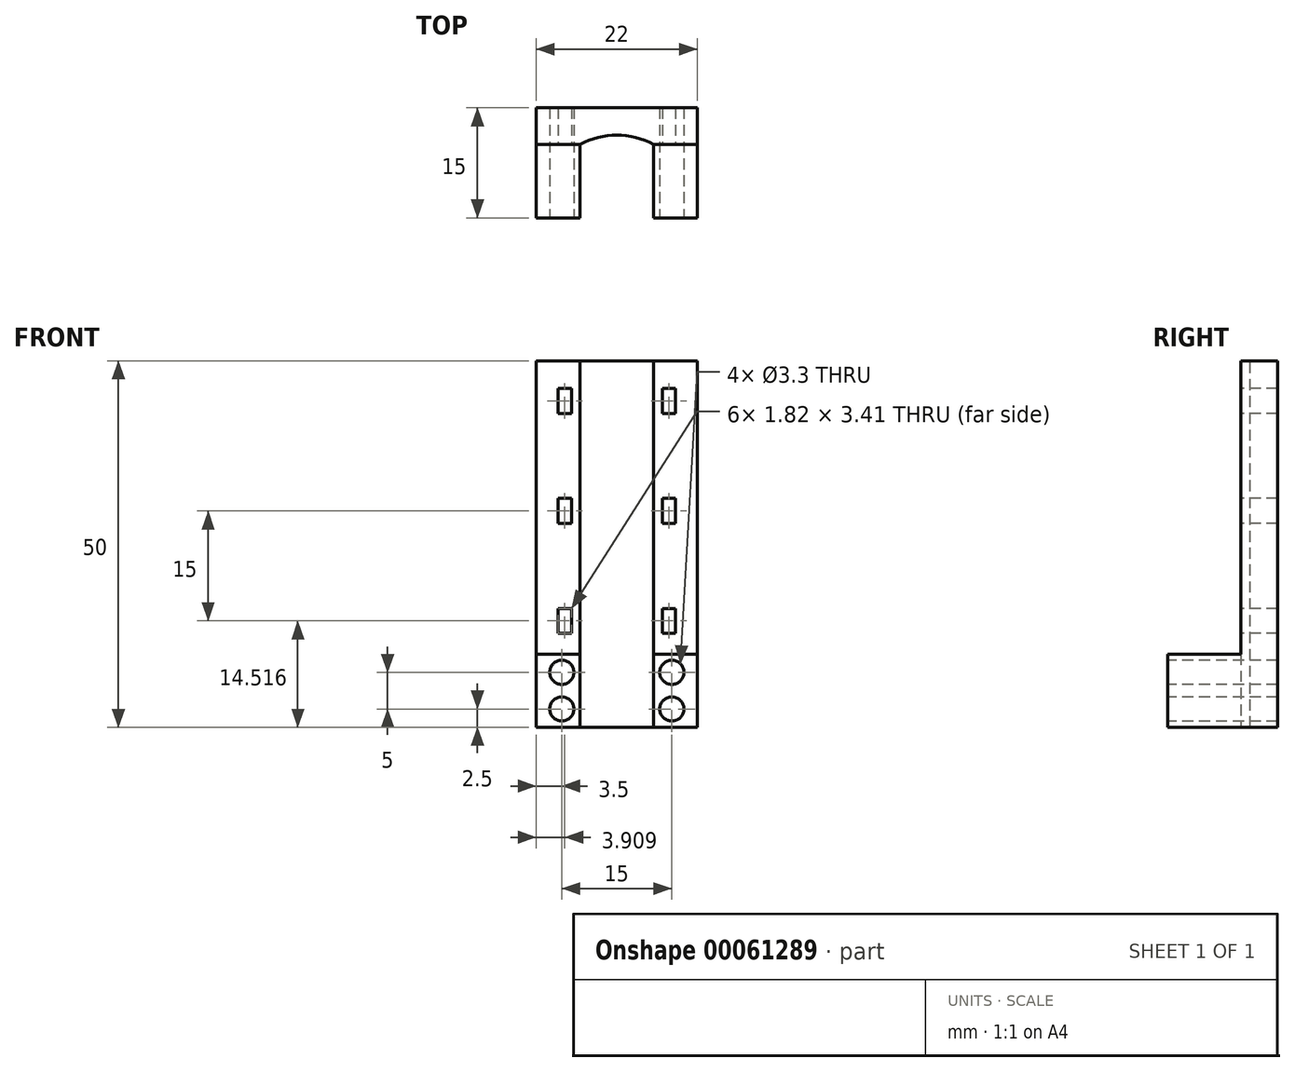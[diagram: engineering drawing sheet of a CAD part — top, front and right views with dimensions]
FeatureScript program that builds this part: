
annotation { "Feature Type Name" : "Feature", "Feature Type Description" : "" }
export const myFeature = defineFeature(function(context is Context, id is Id, definition is map)
    precondition{}
    {
        {
            var Q0;
            Q0=qCreatedBy(makeId("Top.planeOp"),FACE);
            var sketch = newSketch(context, id + "F0", { "sketchPlane" : qUnion([Q0])});
            skLineSegment(sketch, "E0.bottom", {"start": v(0, 0) * mm, "end": v(6, 0) * mm});
            skLineSegment(sketch, "E0.top", {"start": v(0, 15) * mm, "end": v(22, 15) * mm});
            skLineSegment(sketch, "E0.left", {"start": v(0, 0) * mm, "end": v(0, 15) * mm});
            skLineSegment(sketch, "E0.right", {"start": v(22, 0) * mm, "end": v(22, 15) * mm});
            skLineSegment(sketch, "E1.top", {"start": v(6, 10) * mm, "end": v(16, 10) * mm});
            skLineSegment(sketch, "E1.left", {"start": v(6, 0) * mm, "end": v(6, 10) * mm});
            skLineSegment(sketch, "E1.right", {"start": v(16, 0) * mm, "end": v(16, 10) * mm});
            skLineSegment(sketch, "E2.trimOffspring", {"start": v(16, 0) * mm, "end": v(22, 0) * mm});
            skSolve(sketch);
        }
        {
            var Q0;
            Q0 = qSketchRegion(id + "F0", true);
            extrude(context, id + "F1", {"entities" : qUnion([Q0]), "depth" : 10 * mm});
        }
        {
            var Q0;
            Q0=makeQuery(id+"F1.opExtrude","CAP_FACE",FACE,{"disambiguationData":[OSD([sQuery(id+"F0.wireOp",EDGE,"E0.bottom"),sQuery(id+"F0.wireOp",EDGE,"E0.top"),sQuery(id+"F0.wireOp",EDGE,"E0.left"),sQuery(id+"F0.wireOp",EDGE,"E0.right"),sQuery(id+"F0.wireOp",EDGE,"E1.top"),sQuery(id+"F0.wireOp",EDGE,"E1.left"),sQuery(id+"F0.wireOp",EDGE,"E1.right"),sQuery(id+"F0.wireOp",EDGE,"E2.trimOffspring")])],"isStart":false});
            var sketch = newSketch(context, id + "F2", { "sketchPlane" : qUnion([Q0])});
            skLineSegment(sketch, "E3.bottom", {"start": v(0, 15) * mm, "end": v(22, 15) * mm});
            skLineSegment(sketch, "E3.left", {"start": v(0, 15) * mm, "end": v(0, 10) * mm});
            skLineSegment(sketch, "E3.right", {"start": v(22, 15) * mm, "end": v(22, 10) * mm});
            skLineSegment(sketch, "E4", {"start": v(0, 10) * mm, "end": v(22, 10) * mm});
            skSolve(sketch);
        }
        {
            var Q0;
            Q0 = qSketchRegion(id + "F2", true);
            extrude(context, id + "F3", {"entities" : qUnion([Q0]), "operationType" : NewBodyOperationType.ADD, "depth" : 40 * mm});
        }
        {
            var Q0;
            Q0=makeQuery(id+"F3.boolean.opBoolean","MERGE",FACE,{"derivedFrom":[makeQuery(id+"F1.opExtrude","SWEPT_FACE",FACE,{"disambiguationData":[OSD([sQuery(id+"F0.wireOp",EDGE,"E1.top")])]}),makeQuery(id+"F3.opExtrude","SWEPT_FACE",FACE,{"disambiguationData":[OSD([sQuery(id+"F2.wireOp",EDGE,"E4")])]})]});
            var sketch = newSketch(context, id + "F4", { "sketchPlane" : qUnion([Q0])});
            skLineSegment(sketch, "E5", {"start": v(11, 28.2) * mm, "end": v(11, -4.3) * mm, "construction": true});
            skPoint(sketch, "E5.startSnap0", {"position": v(11, 25) * mm});
            skLineSegment(sketch, "E6.bottom", {"start": v(3, 16.22) * mm, "end": v(4.82, 16.22) * mm});
            skLineSegment(sketch, "E6.top", {"start": v(3, 12.81) * mm, "end": v(4.82, 12.81) * mm});
            skLineSegment(sketch, "E6.left", {"start": v(3, 16.22) * mm, "end": v(3, 12.81) * mm});
            skLineSegment(sketch, "E6.right", {"start": v(4.82, 16.22) * mm, "end": v(4.82, 12.81) * mm});
            skLineSegment(sketch, "E7.MirrorCS", {"start": v(19, 12.81) * mm, "end": v(17.18, 12.81) * mm});
            skLineSegment(sketch, "E8.MirrorCS", {"start": v(19, 16.22) * mm, "end": v(17.18, 16.22) * mm});
            skLineSegment(sketch, "E9.MirrorCS", {"start": v(17.18, 16.22) * mm, "end": v(17.18, 12.81) * mm});
            skLineSegment(sketch, "E10.MirrorCS", {"start": v(19, 16.22) * mm, "end": v(19, 12.81) * mm});
            skCircle(sketch, "E11", {"center": v(18.5, 2.5) * mm, "radius": 1.65 * mm});
            skCircle(sketch, "E12.MirrorC", {"center": v(3.5, 2.5) * mm, "radius": 1.65 * mm});
            skLineSegment(sketch, "E13.1.0.0", {"start": v(19, 31.22) * mm, "end": v(19, 27.81) * mm});
            skLineSegment(sketch, "E13.1.0.1", {"start": v(19, 27.81) * mm, "end": v(17.18, 27.81) * mm});
            skLineSegment(sketch, "E13.1.0.2", {"start": v(19, 31.22) * mm, "end": v(17.18, 31.22) * mm});
            skLineSegment(sketch, "E13.1.0.3", {"start": v(17.18, 31.22) * mm, "end": v(17.18, 27.81) * mm});
            skLineSegment(sketch, "E13.1.0.4", {"start": v(11, 43.2) * mm, "end": v(11, 10.7) * mm, "construction": true});
            skLineSegment(sketch, "E13.2.0.0", {"start": v(19, 46.22) * mm, "end": v(19, 42.81) * mm});
            skLineSegment(sketch, "E13.2.0.1", {"start": v(19, 42.81) * mm, "end": v(17.18, 42.81) * mm});
            skLineSegment(sketch, "E13.2.0.2", {"start": v(19, 46.22) * mm, "end": v(17.18, 46.22) * mm});
            skLineSegment(sketch, "E13.2.0.3", {"start": v(17.18, 46.22) * mm, "end": v(17.18, 42.81) * mm});
            skLineSegment(sketch, "E13.2.0.4", {"start": v(11, 58.2) * mm, "end": v(11, 25.7) * mm, "construction": true});
            skLineSegment(sketch, "E13.direction1", {"start": v(19, 12.81) * mm, "end": v(19, 27.81) * mm, "construction": true});
            skLineSegment(sketch, "E14.MirrorCS", {"start": v(3, 27.81) * mm, "end": v(4.82, 27.81) * mm});
            skLineSegment(sketch, "E15.MirrorCS", {"start": v(3, 31.22) * mm, "end": v(4.82, 31.22) * mm});
            skLineSegment(sketch, "E16.MirrorCS", {"start": v(3, 42.81) * mm, "end": v(4.82, 42.81) * mm});
            skLineSegment(sketch, "E17.MirrorCS", {"start": v(3, 46.22) * mm, "end": v(4.82, 46.22) * mm});
            skLineSegment(sketch, "E18.MirrorCS", {"start": v(4.82, 46.22) * mm, "end": v(4.82, 42.81) * mm});
            skLineSegment(sketch, "E19.MirrorCS", {"start": v(3, 31.22) * mm, "end": v(3, 27.81) * mm});
            skLineSegment(sketch, "E20.MirrorCS", {"start": v(3, 46.22) * mm, "end": v(3, 42.81) * mm});
            skLineSegment(sketch, "E21.MirrorCS", {"start": v(4.82, 31.22) * mm, "end": v(4.82, 27.81) * mm});
            skCircle(sketch, "E22", {"center": v(18.5, 7.5) * mm, "radius": 1.65 * mm});
            skCircle(sketch, "E23.MirrorC", {"center": v(3.5, 7.5) * mm, "radius": 1.65 * mm});
            skSolve(sketch);
        }
        {
            var Q0;
            Q0 = qSketchRegion(id + "F4", true);
            extrude(context, id + "F5", {"entities" : qUnion([Q0]), "operationType" : NewBodyOperationType.REMOVE, "oppositeDirection" : true, "depth" : 25 * mm, "hasSecondDirection" : true, "secondDirectionOppositeDirection" : false, "secondDirectionDepth" : 25 * mm});
        }
        {
            var Q0;
            Q0=makeQuery(id+"F3.opExtrude","CAP_FACE",FACE,{"disambiguationData":[OSD([sQuery(id+"F2.wireOp",EDGE,"E3.bottom"),sQuery(id+"F2.wireOp",EDGE,"E3.top"),sQuery(id+"F2.wireOp",EDGE,"E3.left"),sQuery(id+"F2.wireOp",EDGE,"E3.right")])],"isStart":false});
            var sketch = newSketch(context, id + "F6", { "sketchPlane" : qUnion([Q0])});
            skLineSegment(sketch, "E24", {"start": v(11, 2.24) * mm, "end": v(11, 7.63) * mm, "construction": true});
            skPoint(sketch, "E24.startSnap0", {"position": v(11, 5) * mm});
            skPoint(sketch, "E24.endSnap0", {"position": v(11, 15) * mm});
            skArc(sketch, "E25", {"start": v(16, 10) * mm, "mid": v(11, 11.28) * mm, "end": v(6, 10) * mm});
            skLineSegment(sketch, "E26", {"start": v(6, 10) * mm, "end": v(16, 10) * mm});
            skSolve(sketch);
        }
        {
            var Q0;
            Q0 = qSketchRegion(id + "F6", true);
            extrude(context, id + "F7", {"entities" : qUnion([Q0]), "operationType" : NewBodyOperationType.REMOVE, "endBound" : BoundingType.THROUGH_ALL, "oppositeDirection" : true, "depth" : 25 * mm});
        }
    });
